# Revit family: Shower-Shower_Door-KOHLER-Levity-K-706013_1
name_source: partatom
category: Specialty Equipment
revit_build: Autodesk Revit 2015 (Build: 20140606_1530(x64)
units: mm (PartAtom-declared; Revit-internal decimal feet)

## types (4) — shared parameters
ADA Compliant = No
Assembly Code = C1030200
Date Modified = 10/31/2018
Default Elevation = 0"
Description = Sliding shower door, 82 inch H x 56-5/8 - 59-5/8 inch W, with 3/8 inch thick Crystal Clear glass and blade handles
Glass Material = Kohler-Glass-L-Crystal_Clear
Height = 82"
Length = 3 1/16"
Manufacturer = KOHLER Co.
MasterFormat 1995 = 10820
MasterFormat 2004 = 10.28.13
Material = Anodized Aluminum
Product Documentation Link = http://www.us.kohler.com
Product Name = Levity
Product Page URL = http://www.us.kohler.com
URL = https://www.us.kohler.com

## per-type parameters (varying)
| type | Finish | Model | Type |
| SHP - Bright Polished Silver | Kohler-Metal-SHP-Bright_Polished_Silver | K-706013-L-SHP | 1 |
| NX - Brushed Nickel | Kohler-Metal-NX-Brushed_Nickel | K-706013-L-NX | 2 |
| ABV - Anodized Brushed Bronze | Kohler-Metal-ABV-Anodized_Brushed_Bronze | K-706013-L-ABV | 3 |
| ABZ - Anodized Dark Bronze | Kohler-Metal-ABZ-Anodized_Dark_Bronze | K-706013-L-ABZ | 4 |

## geometry (parser evidence)
native form markers: Sweep x6
no freeform markers — native parametric forms only
